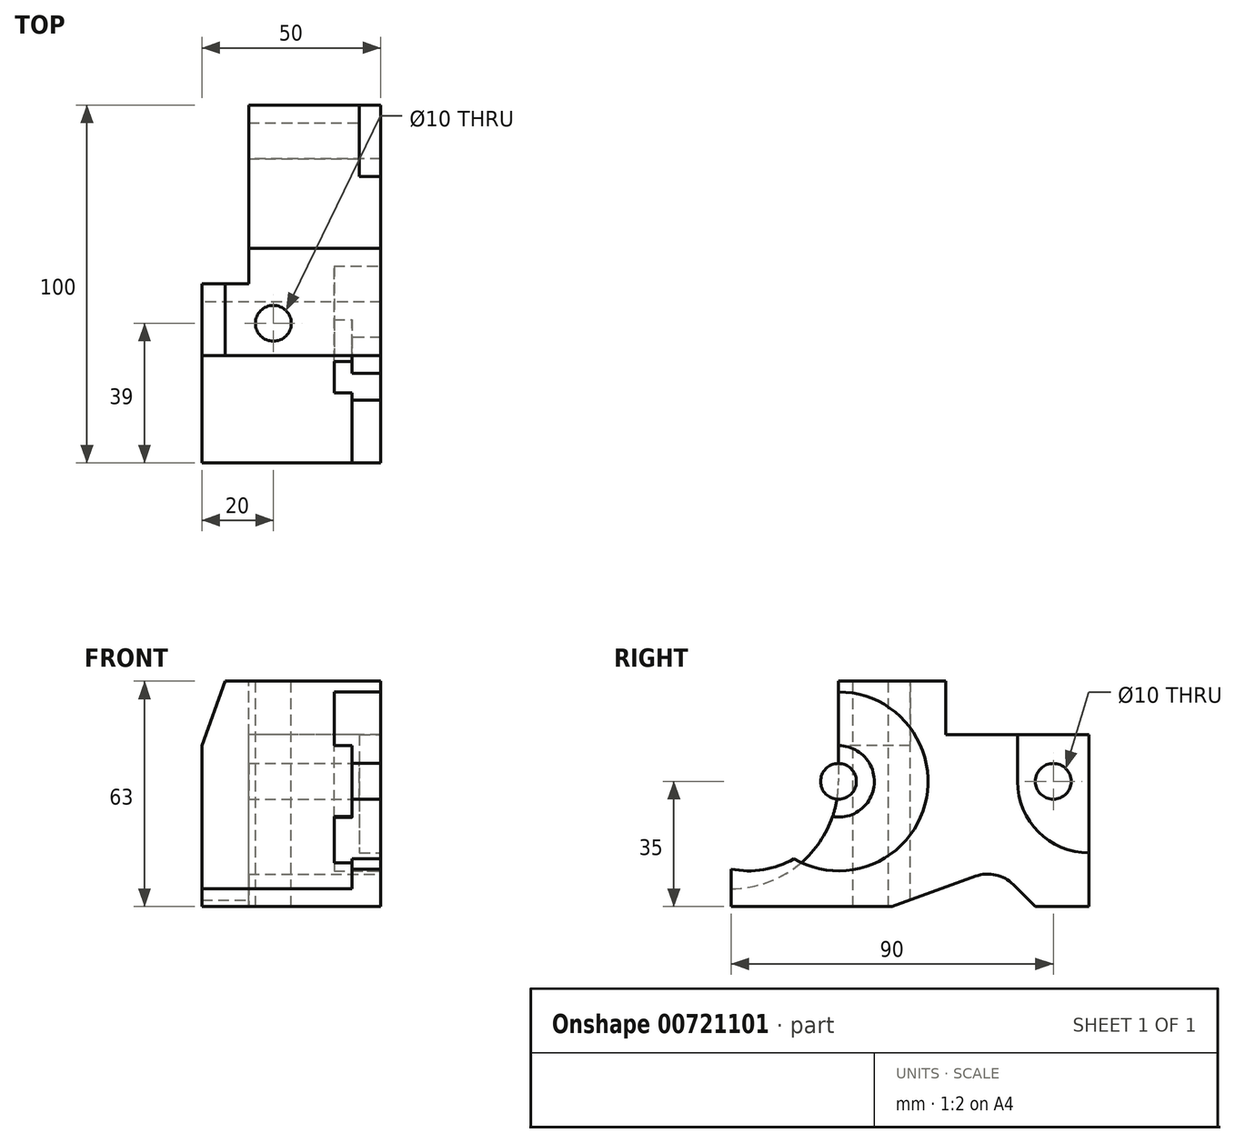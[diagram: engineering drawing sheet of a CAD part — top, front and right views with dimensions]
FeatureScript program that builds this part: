
annotation { "Feature Type Name" : "Feature", "Feature Type Description" : "" }
export const myFeature = defineFeature(function(context is Context, id is Id, definition is map)
    precondition{}
    {
        {
            var Q0;
            Q0=qCreatedBy(makeId("Right.planeOp"),FACE);
            var sketch = newSketch(context, id + "F0", { "sketchPlane" : qUnion([Q0])});
            skLineSegment(sketch, "E0", {"start": v(0, 0) * mm, "end": v(0, 63) * mm});
            skLineSegment(sketch, "E1", {"start": v(0, 63) * mm, "end": v(60, 63) * mm});
            skLineSegment(sketch, "E2", {"start": v(60, 63) * mm, "end": v(60, 48) * mm});
            skLineSegment(sketch, "E3", {"start": v(60, 48) * mm, "end": v(100, 48) * mm});
            skLineSegment(sketch, "E4", {"start": v(100, 48) * mm, "end": v(100, 0) * mm});
            skLineSegment(sketch, "E5", {"start": v(100, 0) * mm, "end": v(85, 0) * mm});
            skLineSegment(sketch, "E6", {"start": v(85, 0) * mm, "end": v(74.33, 10.67) * mm});
            skLineSegment(sketch, "E7", {"start": v(74.33, 10.67) * mm, "end": v(45, 0) * mm});
            skLineSegment(sketch, "E8", {"start": v(45, 0) * mm, "end": v(0, 0) * mm});
            skSolve(sketch);
        }
        {
            var Q0;
            Q0=makeQuery(id+"F0.imprint","IMPRINT",FACE,{"disambiguationData":[TD([[makeQuery(id+"F0.imprint","IMPRINT",EDGE,{"derivedFrom":sQuery(id+"F0.wireOp",EDGE,"E0")}),-1.0]])]});
            extrude(context, id + "F1", {"entities" : qUnion([Q0]), "endBound" : BoundingType.SYMMETRIC, "depth" : 50 * mm, "offsetDistance" : 25 * mm});
        }
        {
            var Q0;
            Q0=makeQuery(id+"F1.opExtrude","CAP_FACE",FACE,{"disambiguationData":[OSD([sQuery(id+"F0.wireOp",EDGE,"E0"),sQuery(id+"F0.wireOp",EDGE,"E1"),sQuery(id+"F0.wireOp",EDGE,"E2"),sQuery(id+"F0.wireOp",EDGE,"E3"),sQuery(id+"F0.wireOp",EDGE,"E4"),sQuery(id+"F0.wireOp",EDGE,"E5"),sQuery(id+"F0.wireOp",EDGE,"E6"),sQuery(id+"F0.wireOp",EDGE,"E7"),sQuery(id+"F0.wireOp",EDGE,"E8")])],"isStart":true});
            var sketch = newSketch(context, id + "F2", { "sketchPlane" : qUnion([Q0])});
            skLineSegment(sketch, "E9", {"start": v(-30, 63) * mm, "end": v(-30, 35) * mm});
            skArc(sketch, "E10", {"start": v(-30, 35) * mm, "mid": v(-21.21, 13.79) * mm, "end": v(0, 5) * mm});
            skLineSegment(sketch, "E11.0", {"start": v(0, 63) * mm, "end": v(-30, 63) * mm});
            skLineSegment(sketch, "E12.0", {"start": v(0, 5) * mm, "end": v(0, 63) * mm});
            skPoint(sketch, "E13.orphan", {"position": v(0, 0) * mm});
            skPoint(sketch, "E14.orphan", {"position": v(-60, 63) * mm});
            skSolve(sketch);
        }
        {
            var Q0;
            Q0 = qSketchRegion(id + "F2", true);
            var Q1;
            Q1=makeQuery(id+"F1.opExtrude","CAP_FACE",FACE,{"disambiguationData":[OSD([sQuery(id+"F0.wireOp",EDGE,"E0"),sQuery(id+"F0.wireOp",EDGE,"E1"),sQuery(id+"F0.wireOp",EDGE,"E2"),sQuery(id+"F0.wireOp",EDGE,"E3"),sQuery(id+"F0.wireOp",EDGE,"E4"),sQuery(id+"F0.wireOp",EDGE,"E5"),sQuery(id+"F0.wireOp",EDGE,"E6"),sQuery(id+"F0.wireOp",EDGE,"E7"),sQuery(id+"F0.wireOp",EDGE,"E8")])],"isStart":false});
            extrude(context, id + "F3", {"entities" : qUnion([Q0]), "operationType" : NewBodyOperationType.REMOVE, "endBound" : BoundingType.UP_TO_SURFACE, "oppositeDirection" : true, "depth" : 25 * mm, "endBoundEntityFace" : qUnion([Q1]), "hasOffset" : true, "offsetDistance" : 8 * mm});
        }
        {
            var Q0;
            Q0=makeQuery(id+"F1.opExtrude","CAP_FACE",FACE,{"disambiguationData":[OSD([sQuery(id+"F0.wireOp",EDGE,"E0"),sQuery(id+"F0.wireOp",EDGE,"E1"),sQuery(id+"F0.wireOp",EDGE,"E2"),sQuery(id+"F0.wireOp",EDGE,"E3"),sQuery(id+"F0.wireOp",EDGE,"E4"),sQuery(id+"F0.wireOp",EDGE,"E5"),sQuery(id+"F0.wireOp",EDGE,"E6"),sQuery(id+"F0.wireOp",EDGE,"E7"),sQuery(id+"F0.wireOp",EDGE,"E8")])],"isStart":false});
            var sketch = newSketch(context, id + "F4", { "sketchPlane" : qUnion([Q0])});
            skLineSegment(sketch, "E15", {"start": v(30, 63) * mm, "end": v(30, 35) * mm});
            skArc(sketch, "E16", {"start": v(0, 10.5) * mm, "mid": v(20.81, 15.64) * mm, "end": v(30, 35) * mm});
            skLineSegment(sketch, "E17.0", {"start": v(0, 63) * mm, "end": v(30, 63) * mm});
            skLineSegment(sketch, "E18.0", {"start": v(0, 10.5) * mm, "end": v(0, 63) * mm});
            skPoint(sketch, "E19.orphan", {"position": v(60, 63) * mm});
            skPoint(sketch, "E20.orphan", {"position": v(0, 0) * mm});
            skSolve(sketch);
        }
        {
            var Q0;
            Q0 = qSketchRegion(id + "F4", true);
            extrude(context, id + "F5", {"entities" : qUnion([Q0]), "operationType" : NewBodyOperationType.REMOVE, "oppositeDirection" : true, "depth" : 25 * mm, "offsetDistance" : 25 * mm});
        }
        {
            var Q0;
            Q0=makeQuery(id+"F1.opExtrude","CAP_FACE",FACE,{"disambiguationData":[OSD([sQuery(id+"F0.wireOp",EDGE,"E0"),sQuery(id+"F0.wireOp",EDGE,"E1"),sQuery(id+"F0.wireOp",EDGE,"E2"),sQuery(id+"F0.wireOp",EDGE,"E3"),sQuery(id+"F0.wireOp",EDGE,"E4"),sQuery(id+"F0.wireOp",EDGE,"E5"),sQuery(id+"F0.wireOp",EDGE,"E6"),sQuery(id+"F0.wireOp",EDGE,"E7"),sQuery(id+"F0.wireOp",EDGE,"E8")])],"isStart":false});
            var sketch = newSketch(context, id + "F6", { "sketchPlane" : qUnion([Q0])});
            skCircle(sketch, "E21", {"center": v(30, 35) * mm, "radius": 10 * mm});
            skCircle(sketch, "E22", {"center": v(30, 35) * mm, "radius": 25 * mm});
            skCircle(sketch, "E23", {"center": v(30, 35) * mm, "radius": 5 * mm});
            skSolve(sketch);
        }
        {
            var Q0;
            Q0 = qSketchRegion(id + "F6", true);
            extrude(context, id + "F7", {"entities" : qUnion([Q0]), "operationType" : NewBodyOperationType.REMOVE, "oppositeDirection" : true, "depth" : 13 * mm, "offsetDistance" : 25 * mm});
        }
        {
            var Q0;
            {var subQ0=sQuery(id+"F6.wireOp",EDGE,"E21");var subQ1=makeQuery(id+"F5.boolean.opBoolean","COPY",EDGE,{"derivedFrom":makeQuery(id+"F5.opExtrude","CAP_EDGE",EDGE,{"disambiguationData":[OSD([sQuery(id+"F4.wireOp",EDGE,"E15")])],"isStart":true})});var subQ2=makeQuery(id+"F6.imprint","INTERSECT",VERTEX,{"derivedFrom":[subQ1,subQ0]});Q0=makeQuery(id+"F6.imprint","IMPRINT",FACE,{"disambiguationData":[TD([[makeQuery(id+"F6.imprint","IMPRINT",EDGE,{"disambiguationData":[TD([[subQ2,1.0]])],"derivedFrom":subQ0}),1.0]])]});}
            var Q1;
            {var subQ0=sQuery(id+"F6.wireOp",EDGE,"E21");var subQ1=makeQuery(id+"F5.boolean.opBoolean","COPY",EDGE,{"derivedFrom":makeQuery(id+"F5.opExtrude","CAP_EDGE",EDGE,{"disambiguationData":[OSD([sQuery(id+"F4.wireOp",EDGE,"E15")])],"isStart":true})});var subQ2=makeQuery(id+"F6.imprint","INTERSECT",VERTEX,{"derivedFrom":[subQ1,subQ0]});Q1=makeQuery(id+"F6.imprint","IMPRINT",FACE,{"disambiguationData":[TD([[makeQuery(id+"F6.imprint","IMPRINT",EDGE,{"disambiguationData":[TD([[subQ2,-1.0]])],"derivedFrom":subQ0}),1.0]])]});}
            var Q2;
            {var subQ0=sQuery(id+"F6.wireOp",EDGE,"E23");var subQ1=makeQuery(id+"F5.boolean.opBoolean","COPY",EDGE,{"derivedFrom":makeQuery(id+"F5.opExtrude","CAP_EDGE",EDGE,{"disambiguationData":[OSD([sQuery(id+"F4.wireOp",EDGE,"E15")])],"isStart":true})});var subQ2=makeQuery(id+"F6.imprint","INTERSECT",VERTEX,{"derivedFrom":[subQ1,subQ0]});Q2=makeQuery(id+"F6.imprint","IMPRINT",FACE,{"disambiguationData":[TD([[makeQuery(id+"F6.imprint","IMPRINT",EDGE,{"disambiguationData":[TD([[subQ2,-1.0]])],"derivedFrom":subQ0}),1.0]])]});}
            var Q3;
            {var subQ0=sQuery(id+"F6.wireOp",EDGE,"E23");var subQ1=makeQuery(id+"F5.boolean.opBoolean","COPY",EDGE,{"derivedFrom":makeQuery(id+"F5.opExtrude","CAP_EDGE",EDGE,{"disambiguationData":[OSD([sQuery(id+"F4.wireOp",EDGE,"E15")])],"isStart":true})});var subQ2=makeQuery(id+"F6.imprint","INTERSECT",VERTEX,{"derivedFrom":[subQ1,subQ0]});Q3=makeQuery(id+"F6.imprint","IMPRINT",FACE,{"disambiguationData":[TD([[makeQuery(id+"F6.imprint","IMPRINT",EDGE,{"disambiguationData":[TD([[subQ2,1.0]])],"derivedFrom":subQ0}),1.0]])]});}
            extrude(context, id + "F8", {"entities" : qUnion([Q0, Q1, Q2, Q3]), "operationType" : NewBodyOperationType.REMOVE, "oppositeDirection" : true, "depth" : 8 * mm, "offsetDistance" : 25 * mm});
        }
        {
            var Q0;
            Q0=makeQuery(id+"F8.boolean.opBoolean","COPY",FACE,{"derivedFrom":makeQuery(id+"F8.opExtrude","CAP_FACE",FACE,{"disambiguationData":[OSD([sQuery(id+"F6.wireOp",EDGE,"E21")])],"isStart":false})});
            var sketch = newSketch(context, id + "F9", { "sketchPlane" : qUnion([Q0])});
            skCircle(sketch, "E24", {"center": v(30, 35) * mm, "radius": 5 * mm});
            skSolve(sketch);
        }
        {
            var Q0;
            Q0 = qSketchRegion(id + "F9", true);
            extrude(context, id + "F10", {"entities" : qUnion([Q0]), "operationType" : NewBodyOperationType.ADD, "depth" : 8 * mm, "offsetDistance" : 25 * mm});
        }
        {
            var Q0;
            Q0=makeQuery(id+"F5.boolean.opBoolean","MERGE",FACE,{"derivedFrom":[makeQuery(id+"F3.boolean.opBoolean","COPY",FACE,{"derivedFrom":makeQuery(id+"F3.opExtrude","SWEPT_FACE",FACE,{"disambiguationData":[OSD([sQuery(id+"F2.wireOp",EDGE,"E9")])]})}),makeQuery(id+"F5.opExtrude","SWEPT_FACE",FACE,{"disambiguationData":[OSD([sQuery(id+"F4.wireOp",EDGE,"E15")])]})]});
            var sketch = newSketch(context, id + "F11", { "sketchPlane" : qUnion([Q0])});
            skLineSegment(sketch, "E25", {"start": v(-18.45, 63) * mm, "end": v(-25, 45) * mm});
            skLineSegment(sketch, "E26.0", {"start": v(-25, 63) * mm, "end": v(-25, 45) * mm});
            skLineSegment(sketch, "E27.0", {"start": v(-18.45, 63) * mm, "end": v(-25, 63) * mm});
            skPoint(sketch, "E28.orphan", {"position": v(25, 63) * mm});
            skPoint(sketch, "E29.orphan", {"position": v(-25, 35) * mm});
            skSolve(sketch);
        }
        {
            var Q0;
            Q0 = qSketchRegion(id + "F11", true);
            extrude(context, id + "F12", {"entities" : qUnion([Q0]), "operationType" : NewBodyOperationType.REMOVE, "endBound" : BoundingType.THROUGH_ALL, "oppositeDirection" : true, "depth" : 25 * mm, "offsetDistance" : 25 * mm});
        }
        {
            var Q0;
            Q0=makeQuery(id+"F1.opExtrude","SWEPT_FACE",FACE,{"disambiguationData":[OSD([sQuery(id+"F0.wireOp",EDGE,"E1")])]});
            var sketch = newSketch(context, id + "F13", { "sketchPlane" : qUnion([Q0])});
            skCircle(sketch, "E30", {"center": v(-5, 39) * mm, "radius": 5 * mm});
            skSolve(sketch);
        }
        {
            var Q0;
            Q0 = qSketchRegion(id + "F13", true);
            extrude(context, id + "F14", {"entities" : qUnion([Q0]), "operationType" : NewBodyOperationType.REMOVE, "endBound" : BoundingType.THROUGH_ALL, "oppositeDirection" : true, "depth" : 25 * mm, "offsetDistance" : 25 * mm});
        }
        {
            var Q0;
            {var subQ0=sQuery(id+"F0.wireOp",EDGE,"E8");var subQ1=sQuery(id+"F0.wireOp",EDGE,"E7");var subQ2=sQuery(id+"F0.wireOp",EDGE,"E6");var subQ3=sQuery(id+"F0.wireOp",EDGE,"E5");var subQ4=sQuery(id+"F0.wireOp",EDGE,"E4");var subQ5=sQuery(id+"F0.wireOp",EDGE,"E0");var subQ6=sQuery(id+"F0.wireOp",EDGE,"E3");var subQ7=sQuery(id+"F0.wireOp",EDGE,"E1");var subQ8=sQuery(id+"F0.wireOp",EDGE,"E2");Q0=makeQuery(id+"F7.boolean.opBoolean","SPLIT",FACE,{"disambiguationData":[TD([makeQuery(id+"F1.opExtrude","SWEPT_FACE",FACE,{"disambiguationData":[OSD([subQ5])]})])],"derivedFrom":makeQuery(id+"F1.opExtrude","CAP_FACE",FACE,{"disambiguationData":[OSD([subQ5,subQ7,subQ8,subQ6,subQ4,subQ3,subQ2,subQ1,subQ0])],"isStart":false})});}
            var sketch = newSketch(context, id + "F15", { "sketchPlane" : qUnion([Q0])});
            skLineSegment(sketch, "E31", {"start": v(80, 48) * mm, "end": v(80, 35) * mm});
            skArc(sketch, "E32", {"start": v(80, 35) * mm, "mid": v(85.86, 20.86) * mm, "end": v(100, 15) * mm});
            skLineSegment(sketch, "E33.0", {"start": v(80, 48) * mm, "end": v(100, 48) * mm});
            skLineSegment(sketch, "E34.0", {"start": v(100, 48) * mm, "end": v(100, 15) * mm});
            skPoint(sketch, "E35.orphan", {"position": v(100, 0) * mm});
            skPoint(sketch, "E36.orphan", {"position": v(60, 48) * mm});
            skSolve(sketch);
        }
        {
            var Q0;
            Q0 = qSketchRegion(id + "F15", true);
            extrude(context, id + "F16", {"entities" : qUnion([Q0]), "operationType" : NewBodyOperationType.REMOVE, "oppositeDirection" : true, "depth" : 6 * mm, "offsetDistance" : 25 * mm});
        }
        {
            var Q0;
            Q0=makeQuery(id+"F16.boolean.opBoolean","COPY",FACE,{"derivedFrom":makeQuery(id+"F16.opExtrude","CAP_FACE",FACE,{"disambiguationData":[OSD([sQuery(id+"F15.wireOp",EDGE,"E31"),sQuery(id+"F15.wireOp",EDGE,"E32"),sQuery(id+"F15.wireOp",EDGE,"E33.0"),sQuery(id+"F15.wireOp",EDGE,"E34.0")])],"isStart":false})});
            var sketch = newSketch(context, id + "F17", { "sketchPlane" : qUnion([Q0])});
            skCircle(sketch, "E37", {"center": v(90, 35) * mm, "radius": 5 * mm});
            skSolve(sketch);
        }
        {
            var Q0;
            Q0 = qSketchRegion(id + "F17", true);
            extrude(context, id + "F18", {"entities" : qUnion([Q0]), "operationType" : NewBodyOperationType.REMOVE, "endBound" : BoundingType.THROUGH_ALL, "oppositeDirection" : true, "depth" : 25 * mm, "offsetDistance" : 25 * mm});
        }
        {
            var Q0;
            Q0=makeQuery(id+"F1.opExtrude","SWEPT_FACE",FACE,{"disambiguationData":[OSD([sQuery(id+"F0.wireOp",EDGE,"E1")])]});
            var sketch = newSketch(context, id + "F19", { "sketchPlane" : qUnion([Q0])});
            skLineSegment(sketch, "E38", {"start": v(-34.74, 110.26) * mm, "end": v(-11.9, 110.26) * mm});
            skLineSegment(sketch, "E39", {"start": v(-11.9, 110.26) * mm, "end": v(-11.9, 50) * mm});
            skLineSegment(sketch, "E40", {"start": v(-11.9, 50) * mm, "end": v(-34.74, 50) * mm});
            skLineSegment(sketch, "E41", {"start": v(-34.74, 50) * mm, "end": v(-34.74, 110.26) * mm});
            skSolve(sketch);
        }
        {
            var Q0;
            Q0 = qSketchRegion(id + "F19", true);
            extrude(context, id + "F20", {"entities" : qUnion([Q0]), "operationType" : NewBodyOperationType.REMOVE, "endBound" : BoundingType.THROUGH_ALL, "oppositeDirection" : true, "depth" : 25 * mm, "offsetDistance" : 25 * mm});
        }
        {
            var Q0;
            Q0=makeQuery(id+"F1.opExtrude","SWEPT_EDGE",EDGE,{"disambiguationData":[OSD([sQuery(id+"F0.wireOp",EDGE,"E6"),sQuery(id+"F0.wireOp",EDGE,"E7")])]});
            fillet(context, id + "F21", {"entities" : qUnion([Q0]), "radius" : 10 * mm, "tangentPropagation" : true, "allowEdgeOverflow" : false});
        }
    });
